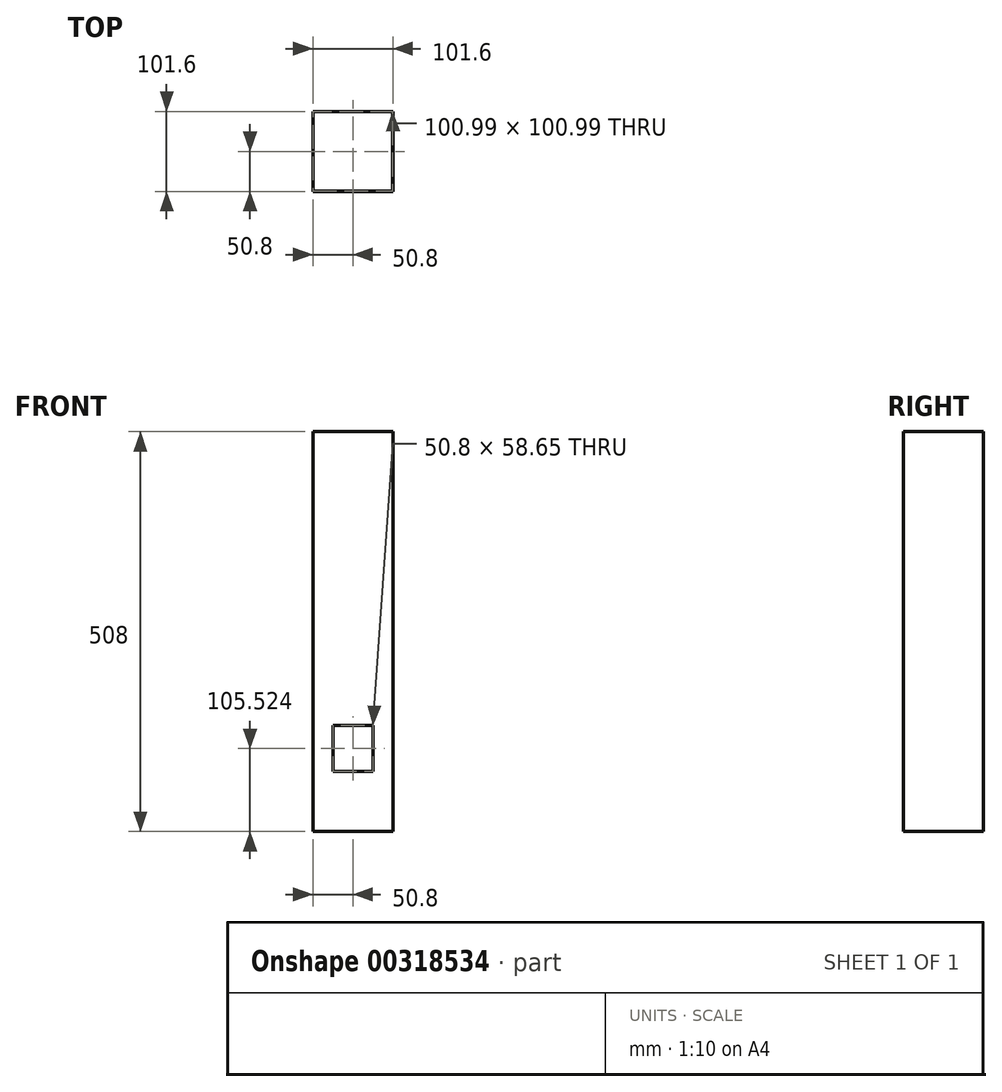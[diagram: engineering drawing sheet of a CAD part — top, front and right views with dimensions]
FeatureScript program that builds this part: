
annotation { "Feature Type Name" : "Feature", "Feature Type Description" : "" }
export const myFeature = defineFeature(function(context is Context, id is Id, definition is map)
    precondition{}
    {
        {
            var Q0;
            Q0=qCreatedBy(makeId("Top.planeOp"),FACE);
            var sketch = newSketch(context, id + "F0", { "sketchPlane" : qUnion([Q0])});
            skLineSegment(sketch, "E0.bottom", {"start": v(50.8, -50.8) * mm, "end": v(-50.8, -50.8) * mm});
            skLineSegment(sketch, "E0.top", {"start": v(50.8, 50.8) * mm, "end": v(-50.8, 50.8) * mm});
            skLineSegment(sketch, "E0.left", {"start": v(50.8, -50.8) * mm, "end": v(50.8, 50.8) * mm});
            skLineSegment(sketch, "E0.right", {"start": v(-50.8, -50.8) * mm, "end": v(-50.8, 50.8) * mm});
            skPoint(sketch, "E0.middle", {"position": v(0, 0) * mm});
            skLineSegment(sketch, "E1.bottom", {"start": v(50.5, -50.5) * mm, "end": v(-50.5, -50.5) * mm});
            skLineSegment(sketch, "E1.top", {"start": v(50.5, 50.5) * mm, "end": v(-50.5, 50.5) * mm});
            skLineSegment(sketch, "E1.left", {"start": v(50.5, -50.5) * mm, "end": v(50.5, 50.5) * mm});
            skLineSegment(sketch, "E1.right", {"start": v(-50.5, -50.5) * mm, "end": v(-50.5, 50.5) * mm});
            skSolve(sketch);
        }
        {
            var Q0;
            Q0=makeQuery(id+"F0.imprint","IMPRINT",FACE,{"disambiguationData":[TD([[makeQuery(id+"F0.imprint","IMPRINT",EDGE,{"derivedFrom":sQuery(id+"F0.wireOp",EDGE,"E0.bottom")}),-1.0]])]});
            extrude(context, id + "F1", {"entities" : qUnion([Q0]), "endBound" : BoundingType.SYMMETRIC, "depth" : 508 * mm});
        }
        {
            var Q0;
            Q0=makeQuery(id+"F0.imprint","IMPRINT",FACE,{"disambiguationData":[TD([[makeQuery(id+"F0.imprint","IMPRINT",EDGE,{"derivedFrom":sQuery(id+"F0.wireOp",EDGE,"E1.bottom")}),-1.0]])]});
            extrude(context, id + "F2", {"entities" : qUnion([Q0]), "operationType" : NewBodyOperationType.REMOVE, "endBound" : BoundingType.SYMMETRIC, "oppositeDirection" : true, "depth" : 508 * mm});
        }
        {
            var Q0;
            Q0=makeQuery(id+"F1.opExtrude","SWEPT_FACE",FACE,{"disambiguationData":[OSD([sQuery(id+"F0.wireOp",EDGE,"E0.bottom")])]});
            var sketch = newSketch(context, id + "F3", { "sketchPlane" : qUnion([Q0])});
            skLineSegment(sketch, "E2.bottom", {"start": v(25.4, -177.8) * mm, "end": v(-25.4, -177.8) * mm});
            skLineSegment(sketch, "E2.top", {"start": v(25.4, -119.15) * mm, "end": v(-25.4, -119.15) * mm});
            skLineSegment(sketch, "E2.left", {"start": v(25.4, -177.8) * mm, "end": v(25.4, -119.15) * mm});
            skLineSegment(sketch, "E2.right", {"start": v(-25.4, -177.8) * mm, "end": v(-25.4, -119.15) * mm});
            skPoint(sketch, "E2.middle", {"position": v(0, -148.48) * mm});
            skSolve(sketch);
        }
        {
            var Q0;
            Q0=makeQuery(id+"F3.imprint","IMPRINT",FACE,{"disambiguationData":[TD([[makeQuery(id+"F3.imprint","IMPRINT",EDGE,{"derivedFrom":sQuery(id+"F3.wireOp",EDGE,"E2.bottom")}),-1.0]])]});
            extrude(context, id + "F4", {"entities" : qUnion([Q0]), "operationType" : NewBodyOperationType.REMOVE, "oppositeDirection" : true, "depth" : 0.33 * mm});
        }
    });
